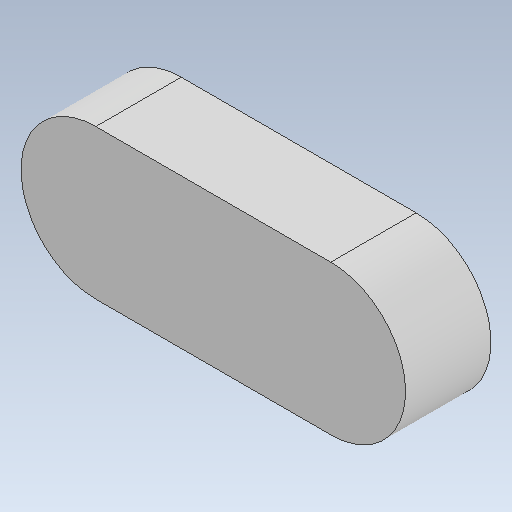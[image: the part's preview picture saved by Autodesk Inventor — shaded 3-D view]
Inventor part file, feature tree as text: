
AUTODESK INVENTOR PART (.ipt)
format: ipt  version: 2020 (Build 240168000, 168)  size: 90,624 bytes
history: native  units: mm
features: other x2, extrude x1, sketch x1, reference x1
ambient origin geometry x8: Origin, YZ Plane, XZ Plane, XY Plane, X Axis, Y Axis, Z Axis, Center Point
bodies: 实体1 (feature_tree)
feature tree (5):
  extrude  "拉伸1"  [1 undecoded]
  sketch  "草图1"  dims[d0=8.0mm d1=0.0mm]
  reference  "参考1"
  other  "<userpath>\Desktop\ME_course_project\课设试试\shaft_try_1.iam"
  other  "shaft_try_1.iam"
note: 1 required parameter value undecoded (feature->parameter linkage not recoverable at this tier; creation-order binding heuristic only, values carry confidence <= 0.55)
